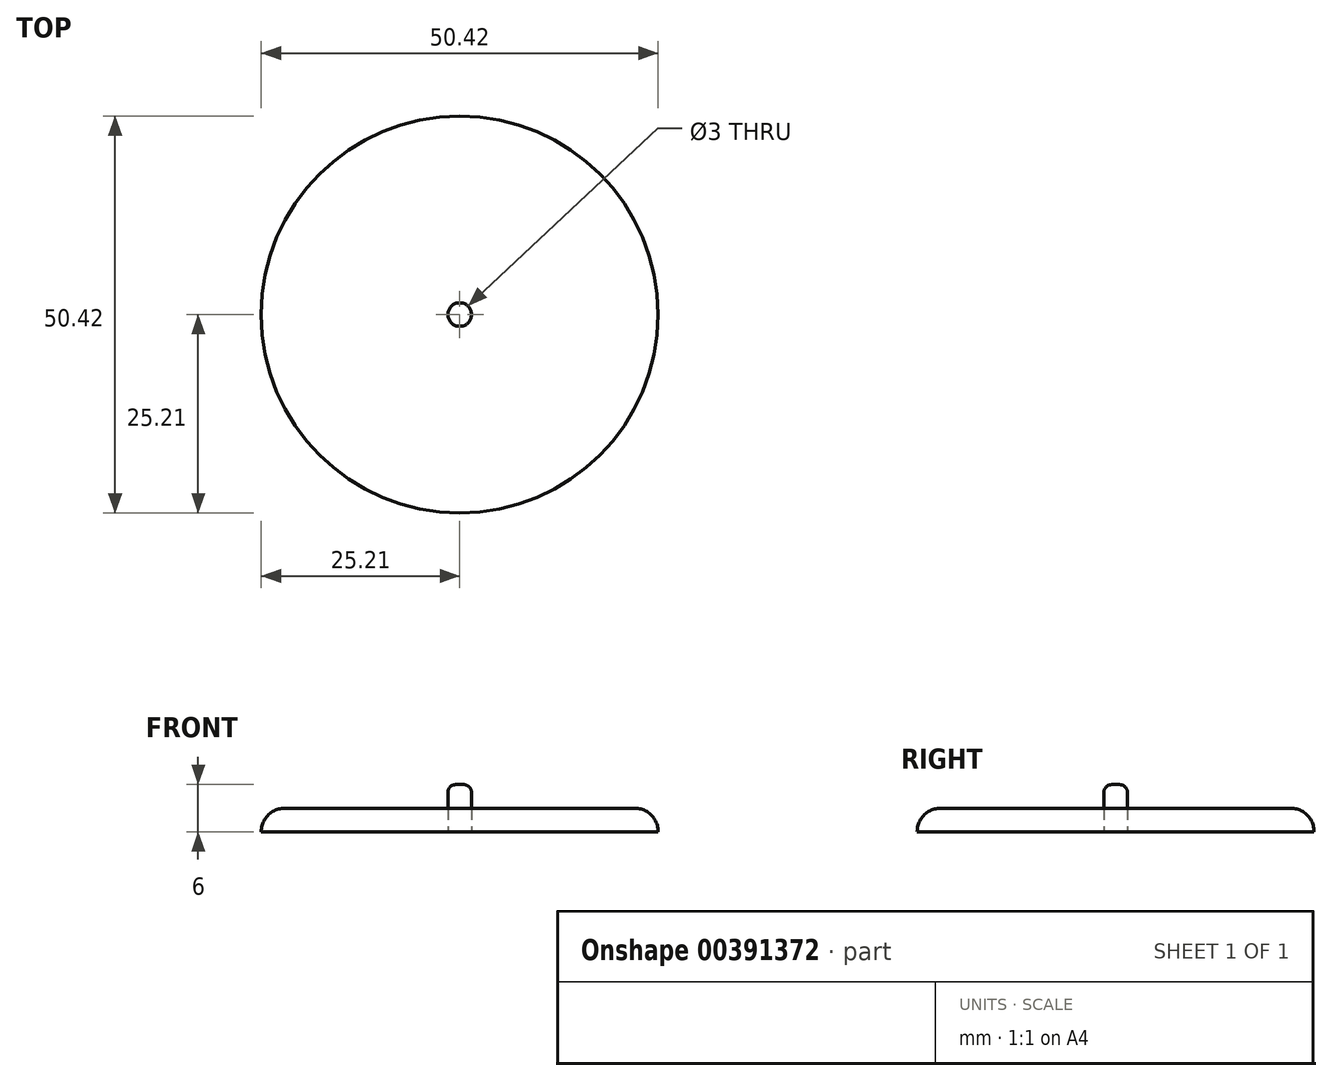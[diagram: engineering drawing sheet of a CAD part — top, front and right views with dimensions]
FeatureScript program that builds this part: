
annotation { "Feature Type Name" : "Feature", "Feature Type Description" : "" }
export const myFeature = defineFeature(function(context is Context, id is Id, definition is map)
    precondition{}
    {
        {
            var Q0;
            Q0=qCreatedBy(makeId("Top.planeOp"),FACE);
            var sketch = newSketch(context, id + "F0", { "sketchPlane" : qUnion([Q0])});
            skCircle(sketch, "E0", {"center": v(-25.4, 0) * mm, "radius": 1.5 * mm});
            skPoint(sketch, "E1.middle", {"position": v(0, 0) * mm});
            skCircle(sketch, "E2", {"center": v(-25.4, 0) * mm, "radius": 25.21 * mm});
            skSolve(sketch);
        }
        {
            var Q0;
            Q0=makeQuery(id+"F0.imprint","IMPRINT",FACE,{"disambiguationData":[TD([[makeQuery(id+"F0.imprint","IMPRINT",EDGE,{"derivedFrom":sQuery(id+"F0.wireOp",EDGE,"E0")}),1.0]])]});
            var Q1;
            Q1=makeQuery(id+"F0.imprint","IMPRINT",FACE,{"disambiguationData":[TD([[makeQuery(id+"F0.imprint","IMPRINT",EDGE,{"derivedFrom":sQuery(id+"F0.wireOp",EDGE,"oNqtisxf-1lKA-D8VF-32i1-kQisSPKeRatL")}),1.0]])]});
            extrude(context, id + "F1", {"entities" : qUnion([Q0, Q1]), "offsetDistance" : 25 * mm, "depth" : 6 * mm});
        }
        {
            var Q0;
            Q0=makeQuery(id+"F0.imprint","IMPRINT",FACE,{"disambiguationData":[TD([[makeQuery(id+"F0.imprint","IMPRINT",EDGE,{"derivedFrom":sQuery(id+"F0.wireOp",EDGE,"E0")}),-1.0]])]});
            extrude(context, id + "F2", {"entities" : qUnion([Q0]), "depth" : 3 * mm, "offsetDistance" : 25 * mm});
        }
        {
            var Q0;
            Q0=makeQuery(id+"F1.opExtrude","CAP_EDGE",EDGE,{"disambiguationData":[OSD([sQuery(id+"F0.wireOp",EDGE,"E0")])],"isStart":false});
            fillet(context, id + "F3", {"entities" : qUnion([Q0]), "radius" : 1 * mm, "tangentPropagation" : true, "allowEdgeOverflow" : false});
        }
        {
            var Q0;
            Q0=makeQuery(id+"F2.opExtrude","CAP_EDGE",EDGE,{"disambiguationData":[OSD([sQuery(id+"F0.wireOp",EDGE,"E2")])],"isStart":false});
            fillet(context, id + "F4", {"entities" : qUnion([Q0]), "radius" : 3 * mm, "tangentPropagation" : true, "allowEdgeOverflow" : false});
        }
    });
